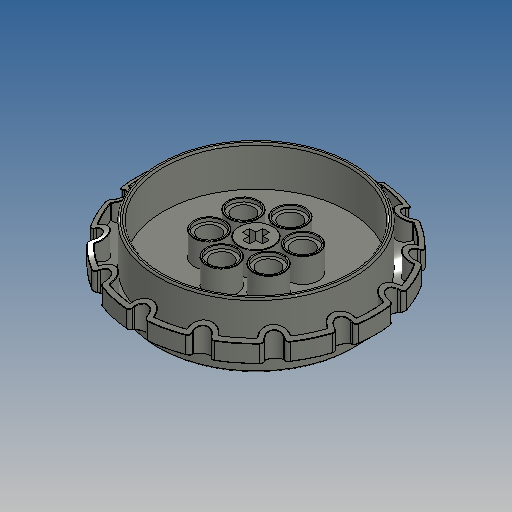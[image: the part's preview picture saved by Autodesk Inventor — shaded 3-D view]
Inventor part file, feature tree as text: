
AUTODESK INVENTOR PART (.ipt)
format: ipt  version: 2025 (Build 290162010, 162A)  size: 1,755,648 bytes
history: native  units: in
note: dims shown in document units (in); Inventor stores cm internally (conversion verified against a paired STEP export)
features: extrude x7, fillet x3, sketch x3, pattern_circular x2, revolve x1, delete_face x1
ambient origin geometry x8: Origin, YZ Plane, XZ Plane, XY Plane, X Axis, Y Axis, Z Axis, Center Point
bodies: Solid1 (feature_tree)
feature tree (17):
  revolve  "Revolution1"  [1 undecoded]
  fillet  "Rundung3"  Radius=0.1575in
  sketch  "Sketch3"  dims[d5=0.315in d6=0.0315in]
  extrude  "Extrusion4"  Depth=0.0315in
  extrude  "Extrusion1"  Depth=1.7008in
  extrude  "Extrusion2"  Depth=2.1969in
  extrude  "Extrusion3"  TaperAngle=90.0deg  [1 undecoded]
  pattern_circular  "Circular Pattern1"  [2 undecoded]
  extrude  "Extrusion5"  Depth=0.0472in
  extrude  "Extrusion6"  Depth=0.189in
  extrude  "Extrusion7"  Depth=0.063in
  delete_face  "Fläche löschen1"
  fillet  "Fillet1"  Radius=0.315in
  pattern_circular  "Circular Pattern2"  [2 undecoded]
  fillet  "Fillet2"  Radius=0.189in
  sketch  "Sketch2"  dims[d1=0.2268in d2=0.315in d4=0.1575in]
  sketch  "Sketch4"  dims[d7=0.9449in d8=1.7008in d10=2.1969in d13=90.0deg d14=0.0472in d16=0.0472in d17=0.189in d18=0.063in d19=0.315in d20=0.2835in d21=0.189in d22=0.252in d23=0.3937in d24=0.0in d25=0.3937in d26=0.0in d27=0.0315in d28=0.0in d29=2.3622in d30=360.0deg d32=0.0315in d33=0.0in d35=0.2835in d36=0.8504in d37=0.1496in d38=0.0315in d39=0.0in d40=22.5deg d42=0.063in d43=0.9986in d44=0.0472in d45=0.0315in d46=0.0in d47=0.0315in d48=0.0in d49=5.5118in d50=360.0deg d52=0.0315in d53=0.0039in d55=0.5906in d56=0.2953in d57=1.7953in d58=0.0472in d59=0.1575in d60=0.1575in d61=0.1306in d62=0.1378in d63=0.1378in d64=0.0157in d65=0.0039in d66=0.4724in d67=0.1767in]
note: 6 required parameter values undecoded (feature->parameter linkage not recoverable at this tier; creation-order binding heuristic only, values carry confidence <= 0.55)